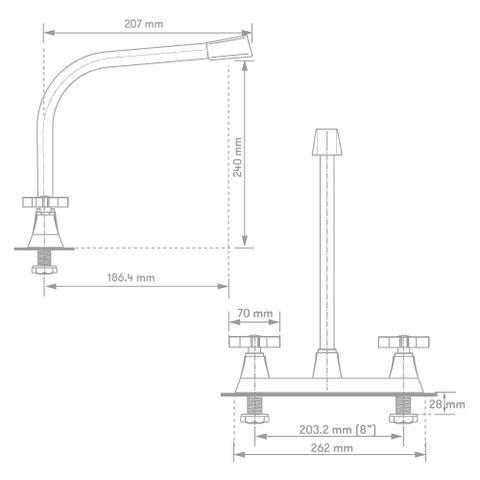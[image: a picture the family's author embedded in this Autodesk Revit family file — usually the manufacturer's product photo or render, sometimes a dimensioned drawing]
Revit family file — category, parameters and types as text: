
# Revit family: 01-3528-11 MEZCLADOR LAVAPLATOS 8 FIRENZE CRUZ
name_source: partatom
category: Aparatos sanitarios
revit_build: Autodesk Revit 2018 (Build: 20170223_1515(x64)
units: mm (PartAtom-declared; Revit-internal decimal feet)

## family parameters
Anfitrión = Cara
Compartido = No
Corte con vacíos al cargar = No
Cota de conector redondo = Diámetro de uso
Número OmniClass = 23.31.11.00
Punto de cálculo de habitación = No
Tipo de pieza = Normal

## types (1)
- 01-3528-11
    Alto brazo = 240 mm  [stored 0.787402 ft]
    Ancho brazo = 207 mm
    Ancho entre manijas = 203.2 mm  [stored 0.666667 ft]
    Ancho manija = 70 mm
    Conexión AC = Sí
    Conexión AF = Sí
    Conexión de residuos = No
    Conexión de ventilación = No
    Descripción = Bimando
    Elevación por defecto = 0 mm  [stored 0 ft]
    Fabricante = Gricol
    Imagen de tipo = <Ninguno>
    Link Ficha Tecnica = http://infotecnica.gricol.com
    Metal Laton Cromado = Metal Laton Cromado
    Metal Zamak Cromado = Metal Zamak Cromado
    Modelo = 01-3528-11
    Plástico - ABS Cromado = Plastico ABS Cromado
    Product Name = MEZCLADOR LAVAPLATOS 8 FIRENZE CRUZ
    URL = https://www.gricol.com

note: [stored X ft] marks values corroborated as IEEE doubles in the binary element streams (Revit-internal decimal feet)

## geometry (parser evidence)
native form markers: Blend x4, Sweep x8
no freeform markers — native parametric forms only
